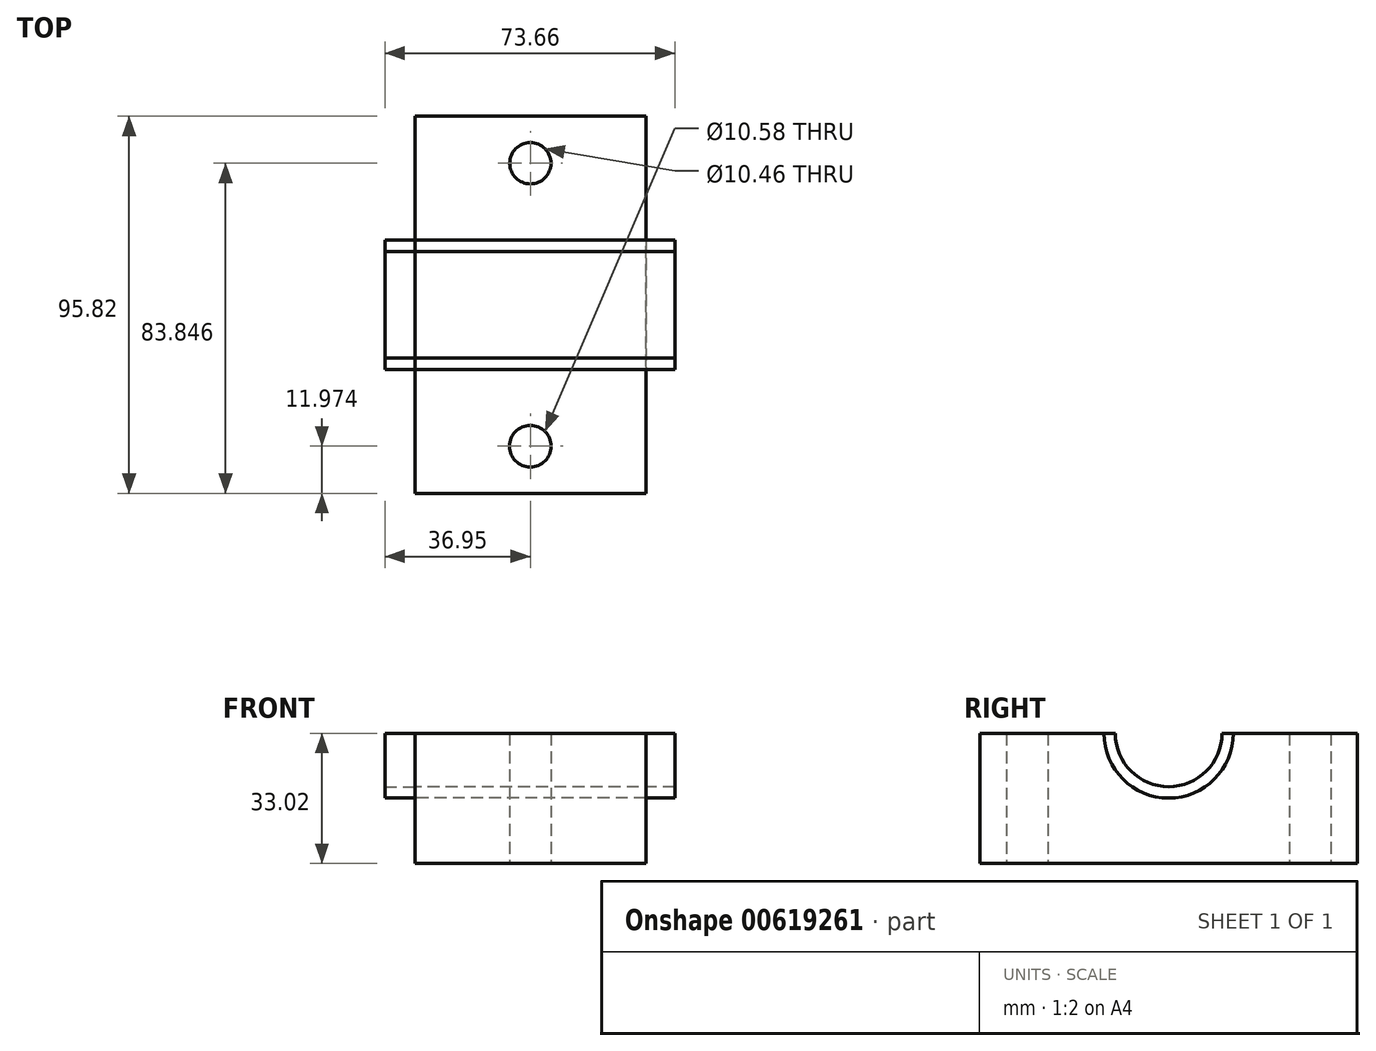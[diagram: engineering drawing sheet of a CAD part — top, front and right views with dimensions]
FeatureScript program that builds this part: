
annotation { "Feature Type Name" : "Feature", "Feature Type Description" : "" }
export const myFeature = defineFeature(function(context is Context, id is Id, definition is map)
    precondition{}
    {
        {
            var Q0;
            Q0=qCreatedBy(makeId("Top.planeOp"),FACE);
            var sketch = newSketch(context, id + "F0", { "sketchPlane" : qUnion([Q0])});
            skLineSegment(sketch, "E0.bottom", {"start": v(29.33, -47.91) * mm, "end": v(-29.33, -47.91) * mm});
            skLineSegment(sketch, "E0.top", {"start": v(29.33, 47.91) * mm, "end": v(-29.33, 47.91) * mm});
            skLineSegment(sketch, "E0.left", {"start": v(29.33, -47.91) * mm, "end": v(29.33, 47.91) * mm});
            skLineSegment(sketch, "E0.right", {"start": v(-29.33, -47.91) * mm, "end": v(-29.33, 47.91) * mm});
            skPoint(sketch, "E0.middle", {"position": v(0, 0) * mm});
            skLineSegment(sketch, "E1", {"start": v(-29.33, 0) * mm, "end": v(0, 0) * mm});
            skLineSegment(sketch, "E2", {"start": v(0, 0) * mm, "end": v(29.33, 0) * mm});
            skLineSegment(sketch, "E3", {"start": v(0, 47.91) * mm, "end": v(0, 0) * mm});
            skLineSegment(sketch, "E4", {"start": v(0, 47.91) * mm, "end": v(0, 23.96) * mm});
            skLineSegment(sketch, "E5", {"start": v(0, -47.91) * mm, "end": v(0, 0) * mm});
            skLineSegment(sketch, "E6", {"start": v(0, -47.91) * mm, "end": v(0, -23.96) * mm});
            skCircle(sketch, "E7", {"center": v(0, 35.94) * mm, "radius": 5.23 * mm});
            skCircle(sketch, "E8", {"center": v(0, -35.94) * mm, "radius": 5.29 * mm});
            skSolve(sketch);
        }
        {
            var Q0;
            Q0 = qSketchRegion(id + "F0", true);
            extrude(context, id + "F1", {"entities" : qUnion([Q0]), "depth" : 33.02 * mm, "offsetDistance" : 25.4 * mm});
        }
        {
            var Q0;
            Q0=makeQuery(id+"F1.opExtrude","SWEPT_FACE",FACE,{"disambiguationData":[OSD([sQuery(id+"F0.wireOp",EDGE,"E0.right")])]});
            var sketch = newSketch(context, id + "F2", { "sketchPlane" : qUnion([Q0])});
            skCircle(sketch, "E9", {"center": v(0, 33.02) * mm, "radius": 16.44 * mm});
            skCircle(sketch, "E10", {"center": v(0, 33.02) * mm, "radius": 13.54 * mm});
            skSolve(sketch);
        }
        {
            var Q0;
            {var subQ0=sQuery(id+"F2.wireOp",EDGE,"E9");var subQ1=makeQuery(id+"F1.opExtrude","CAP_EDGE",EDGE,{"disambiguationData":[OSD([sQuery(id+"F0.wireOp",EDGE,"E0.right")])],"isStart":false});var subQ2=makeQuery(id+"F2.imprint","INTERSECT",VERTEX,{"disambiguationData":[OD(0.0)],"derivedFrom":[subQ1,subQ0]});Q0=makeQuery(id+"F2.imprint","IMPRINT",FACE,{"disambiguationData":[TD([[makeQuery(id+"F2.imprint","IMPRINT",EDGE,{"disambiguationData":[TD([[subQ2,1.0]])],"derivedFrom":subQ0}),1.0]])]});}
            var Q1;
            {var subQ0=sQuery(id+"F2.wireOp",EDGE,"E10");var subQ1=makeQuery(id+"F1.opExtrude","CAP_EDGE",EDGE,{"disambiguationData":[OSD([sQuery(id+"F0.wireOp",EDGE,"E0.right")])],"isStart":false});var subQ2=makeQuery(id+"F2.imprint","INTERSECT",VERTEX,{"disambiguationData":[OD(0.0)],"derivedFrom":[subQ1,subQ0]});Q1=makeQuery(id+"F2.imprint","IMPRINT",FACE,{"disambiguationData":[TD([[makeQuery(id+"F2.imprint","IMPRINT",EDGE,{"disambiguationData":[TD([[subQ2,1.0]])],"derivedFrom":subQ0}),1.0]])]});}
            extrude(context, id + "F3", {"entities" : qUnion([Q0, Q1]), "operationType" : NewBodyOperationType.REMOVE, "oppositeDirection" : true, "depth" : 76.2 * mm, "offsetDistance" : 25.4 * mm});
        }
        {
            var Q0;
            {var subQ0=sQuery(id+"F2.wireOp",EDGE,"E9");var subQ1=makeQuery(id+"F1.opExtrude","CAP_EDGE",EDGE,{"disambiguationData":[OSD([sQuery(id+"F0.wireOp",EDGE,"E0.right")])],"isStart":false});var subQ2=makeQuery(id+"F2.imprint","INTERSECT",VERTEX,{"disambiguationData":[OD(0.0)],"derivedFrom":[subQ1,subQ0]});Q0=makeQuery(id+"F2.imprint","IMPRINT",FACE,{"disambiguationData":[TD([[makeQuery(id+"F2.imprint","IMPRINT",EDGE,{"disambiguationData":[TD([[subQ2,1.0]])],"derivedFrom":subQ0}),1.0]])]});}
            extrude(context, id + "F4", {"entities" : qUnion([Q0]), "depth" : 7.62 * mm, "offsetDistance" : 25.4 * mm});
        }
        {
            var Q0;
            {var subQ0=sQuery(id+"F2.wireOp",EDGE,"E9");var subQ1=makeQuery(id+"F1.opExtrude","CAP_EDGE",EDGE,{"disambiguationData":[OSD([sQuery(id+"F0.wireOp",EDGE,"E0.right")])],"isStart":false});var subQ2=makeQuery(id+"F2.imprint","INTERSECT",VERTEX,{"disambiguationData":[OD(0.0)],"derivedFrom":[subQ1,subQ0]});Q0=makeQuery(id+"F2.imprint","IMPRINT",FACE,{"disambiguationData":[TD([[makeQuery(id+"F2.imprint","IMPRINT",EDGE,{"disambiguationData":[TD([[subQ2,1.0]])],"derivedFrom":subQ0}),1.0]])]});}
            extrude(context, id + "F5", {"entities" : qUnion([Q0]), "oppositeDirection" : true, "depth" : 66.04 * mm, "offsetDistance" : 25.4 * mm});
        }
    });
